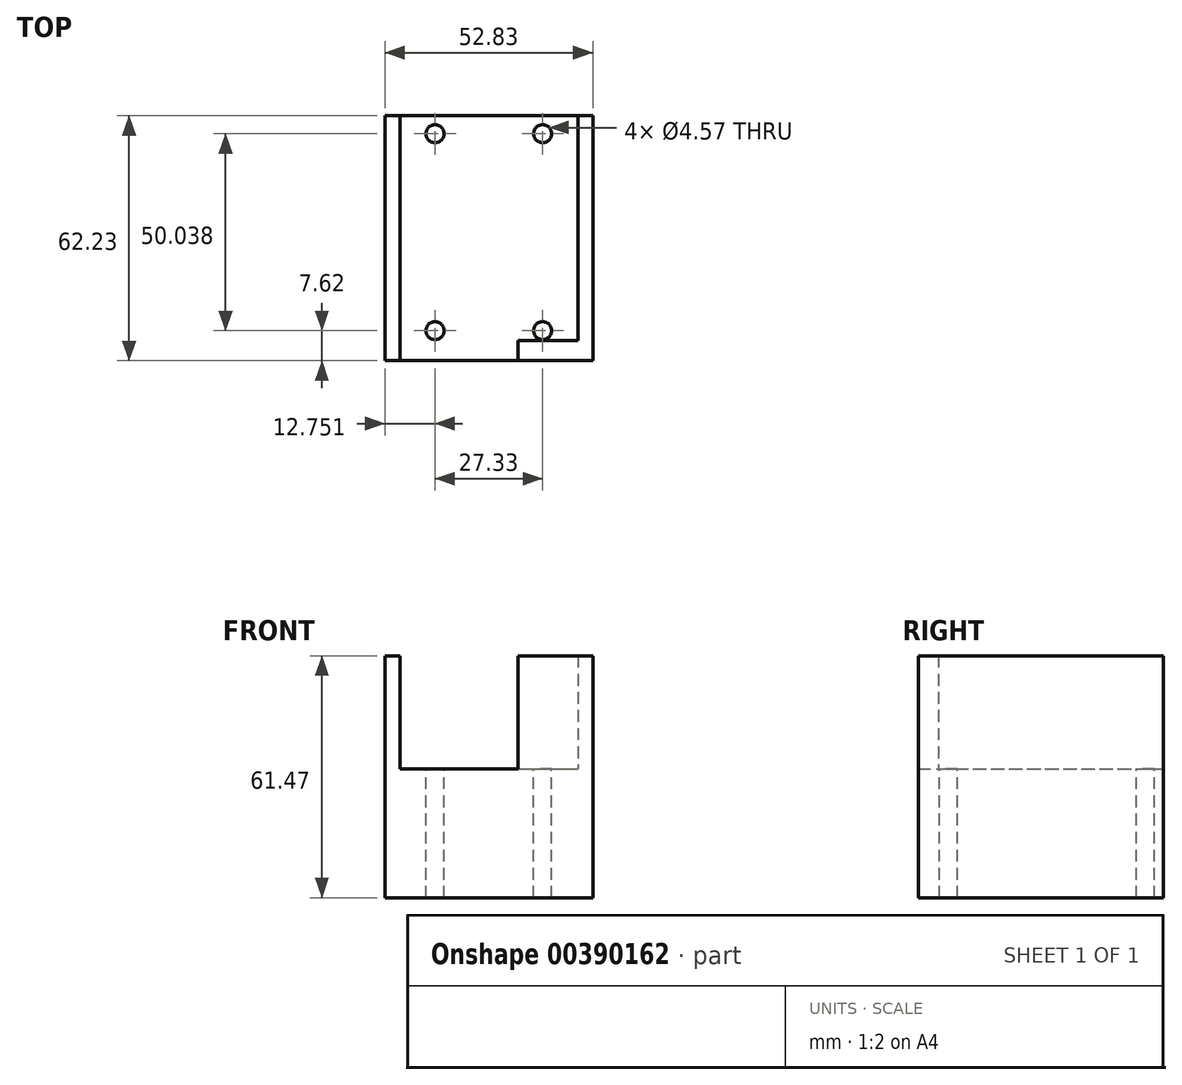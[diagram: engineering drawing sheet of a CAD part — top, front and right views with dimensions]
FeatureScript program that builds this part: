
annotation { "Feature Type Name" : "Feature", "Feature Type Description" : "" }
export const myFeature = defineFeature(function(context is Context, id is Id, definition is map)
    precondition{}
    {
        {
            var Q0;
            Q0=qCreatedBy(makeId("Front.planeOp"),FACE);
            var sketch = newSketch(context, id + "F0", { "sketchPlane" : qUnion([Q0])});
            skLineSegment(sketch, "E0.bottom", {"start": v(0, 32.51) * mm, "end": v(52.83, 32.51) * mm});
            skLineSegment(sketch, "E0.top", {"start": v(0, 0) * mm, "end": v(52.83, 0) * mm});
            skLineSegment(sketch, "E0.left", {"start": v(0, 32.51) * mm, "end": v(0, 0) * mm});
            skLineSegment(sketch, "E0.right", {"start": v(52.83, 32.51) * mm, "end": v(52.83, 0) * mm});
            skSolve(sketch);
        }
        {
            var Q0;
            Q0=qSketchRegion(id+"F0",true);
            extrude(context, id + "F1", {"entities" : qUnion([Q0]), "depth" : 62.23 * mm});
        }
        {
            var Q0;
            Q0=makeQuery(id+"F1.opExtrude","CAP_FACE",FACE,{"disambiguationData":[OSD([sQuery(id+"F0.wireOp",EDGE,"E0.bottom"),sQuery(id+"F0.wireOp",EDGE,"E0.top"),sQuery(id+"F0.wireOp",EDGE,"E0.left"),sQuery(id+"F0.wireOp",EDGE,"E0.right")])],"isStart":true});
            var Q1;
            Q1=makeQuery(id+"F1.opExtrude","SWEPT_FACE",FACE,{"disambiguationData":[OSD([sQuery(id+"F0.wireOp",EDGE,"E0.bottom")])]});
            var Q2;
            Q2=makeQuery(id+"F1.opExtrude","CAP_FACE",FACE,{"disambiguationData":[OSD([sQuery(id+"F0.wireOp",EDGE,"E0.bottom"),sQuery(id+"F0.wireOp",EDGE,"E0.top"),sQuery(id+"F0.wireOp",EDGE,"E0.left"),sQuery(id+"F0.wireOp",EDGE,"E0.right")])],"isStart":false});
            shell(context, id + "F2", {"entities" : qUnion([Q0, Q1, Q2]), "thickness" : 3.8 * mm});
        }
        {
            var Q0;
            Q0=makeQuery(id+"F2.opShell","OFFSET_FACE",FACE,{"disambiguationData":[OSD([sQuery(id+"F0.wireOp",EDGE,"E0.right")])]});
            var sketch = newSketch(context, id + "F3", { "sketchPlane" : qUnion([Q0])});
            skLineSegment(sketch, "E1.bottom", {"start": v(57.15, 32.51) * mm, "end": v(62.23, 32.51) * mm});
            skLineSegment(sketch, "E1.top", {"start": v(57.15, 3.81) * mm, "end": v(62.23, 3.81) * mm});
            skLineSegment(sketch, "E1.left", {"start": v(62.23, 32.51) * mm, "end": v(62.23, 3.8) * mm});
            skLineSegment(sketch, "E1.right", {"start": v(57.15, 32.51) * mm, "end": v(57.15, 3.8) * mm});
            skSolve(sketch);
        }
        {
            var Q0;
            Q0=makeQuery(id+"F3.imprint","IMPRINT",FACE,{"disambiguationData":[TD([[makeQuery(id+"F3.imprint","IMPRINT",EDGE,{"derivedFrom":sQuery(id+"F3.wireOp",EDGE,"E1.bottom")}),1.0]])]});
            extrude(context, id + "F4", {"entities" : qUnion([Q0]), "operationType" : NewBodyOperationType.ADD, "depth" : 15.24 * mm});
        }
        {
            var Q0;
            Q0=makeQuery(id+"F2.opShell","OFFSET_FACE",FACE,{"disambiguationData":[OSD([sQuery(id+"F0.wireOp",EDGE,"E0.top")])]});
            var sketch = newSketch(context, id + "F5", { "sketchPlane" : qUnion([Q0])});
            skPoint(sketch, "E2", {"position": v(12.75, -4.57) * mm});
            skPoint(sketch, "E3", {"position": v(40.08, -4.57) * mm});
            skPoint(sketch, "E4", {"position": v(12.75, -54.61) * mm});
            skPoint(sketch, "E5", {"position": v(40.08, -54.61) * mm});
            skSolve(sketch);
        }
        {
            var Q0;
            Q0=sQuery(id+"F5.wireOp",VERTEX,"E2");
            var Q1;
            Q1=sQuery(id+"F5.wireOp",VERTEX,"E5");
            var Q2;
            Q2=sQuery(id+"F5.wireOp",VERTEX,"E4");
            var Q3;
            Q3=sQuery(id+"F5.wireOp",VERTEX,"E3");
            var Q4;
            Q4=makeQuery(id+"F1.opExtrude","SWEPT_BODY",BODY,{"disambiguationData":[OSD([sQuery(id+"F0.wireOp",EDGE,"E0.bottom"),sQuery(id+"F0.wireOp",EDGE,"E0.top"),sQuery(id+"F0.wireOp",EDGE,"E0.left"),sQuery(id+"F0.wireOp",EDGE,"E0.right")])]});
            hole(context, id + "F6", {"style" : HoleStyle.SIMPLE, "endStyle" : HoleEndStyle.THROUGH, "holeDiameter" : 4.57 * mm, "isTappedThrough" : true, "tappedDepth" : 12.7 * mm, "tapClearance" : 3, "locations" : qUnion([Q0, Q1, Q2, Q3]), "scope" : qUnion([Q4])});
        }
        {
            var Q0;
            Q0=makeQuery(id+"F1.opExtrude","SWEPT_FACE",FACE,{"disambiguationData":[OSD([sQuery(id+"F0.wireOp",EDGE,"E0.top")])]});
            extrude(context, id + "F7", {"entities" : qUnion([Q0]), "operationType" : NewBodyOperationType.ADD, "depth" : 28.96 * mm});
        }
    });
